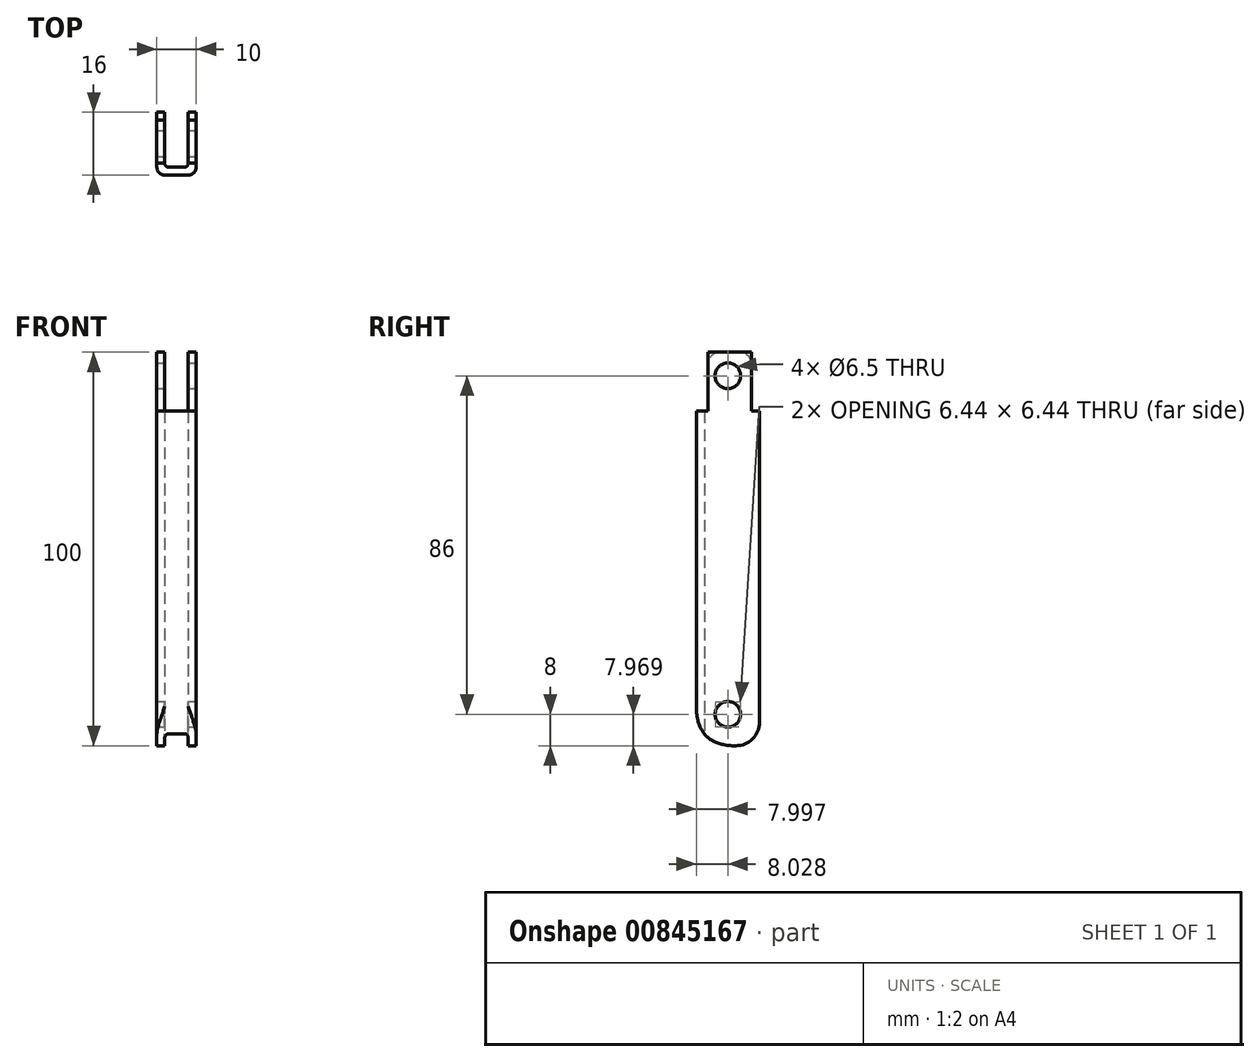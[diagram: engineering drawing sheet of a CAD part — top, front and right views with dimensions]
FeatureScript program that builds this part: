
annotation { "Feature Type Name" : "Feature", "Feature Type Description" : "" }
export const myFeature = defineFeature(function(context is Context, id is Id, definition is map)
    precondition{}
    {
        {
            var Q0;
            Q0=qCreatedBy(makeId("Top.planeOp"),FACE);
            var sketch = newSketch(context, id + "F0", { "sketchPlane" : qUnion([Q0])});
            skLineSegment(sketch, "E0.bottom", {"start": v(-5.2, -4.8) * mm, "end": v(-3.2, -4.8) * mm});
            skLineSegment(sketch, "E0.top", {"start": v(-3.2, -20.8) * mm, "end": v(2.8, -20.8) * mm});
            skLineSegment(sketch, "E0.left", {"start": v(-5.2, -4.8) * mm, "end": v(-5.2, -18.8) * mm});
            skLineSegment(sketch, "E0.right", {"start": v(4.8, -4.8) * mm, "end": v(4.8, -18.8) * mm});
            skLineSegment(sketch, "E1.top", {"start": v(-2.2, -18.8) * mm, "end": v(1.8, -18.8) * mm});
            skLineSegment(sketch, "E1.left", {"start": v(-3.2, -4.8) * mm, "end": v(-3.2, -17.8) * mm});
            skLineSegment(sketch, "E1.right", {"start": v(2.8, -4.8) * mm, "end": v(2.8, -17.8) * mm});
            skPoint(sketch, "E2.visualSharp", {"position": v(-3.2, -18.8) * mm});
            skArc(sketch, "E2.filletArc", {"start": v(-3.2, -17.8) * mm, "mid": v(-2.91, -18.5) * mm, "end": v(-2.2, -18.8) * mm});
            skPoint(sketch, "E3.visualSharp", {"position": v(2.8, -18.8) * mm});
            skArc(sketch, "E3.filletArc", {"start": v(1.8, -18.8) * mm, "mid": v(2.5, -18.5) * mm, "end": v(2.8, -17.8) * mm});
            skPoint(sketch, "E4.visualSharp", {"position": v(-5.2, -20.8) * mm});
            skArc(sketch, "E4.filletArc", {"start": v(-5.2, -18.8) * mm, "mid": v(-4.62, -20.2) * mm, "end": v(-3.2, -20.8) * mm});
            skPoint(sketch, "E5.visualSharp", {"position": v(4.8, -20.8) * mm});
            skArc(sketch, "E5.filletArc", {"start": v(2.8, -20.8) * mm, "mid": v(4.21, -20.2) * mm, "end": v(4.8, -18.8) * mm});
            skLineSegment(sketch, "E6.trimOffspring", {"start": v(2.8, -4.8) * mm, "end": v(4.8, -4.8) * mm});
            skSolve(sketch);
        }
        {
            var Q0;
            Q0 = qSketchRegion(id + "F0", true);
            extrude(context, id + "F1", {"entities" : qUnion([Q0]), "depth" : 100 * mm, "offsetDistance" : 25 * mm});
        }
        {
            var Q0;
            Q0=makeQuery(id+"F1.opExtrude","SWEPT_FACE",FACE,{"disambiguationData":[OSD([sQuery(id+"F0.wireOp",EDGE,"E0.right")])]});
            var sketch = newSketch(context, id + "F2", { "sketchPlane" : qUnion([Q0])});
            skCircle(sketch, "E7", {"center": v(-12.8, 94) * mm, "radius": 3.25 * mm});
            skLineSegment(sketch, "E8", {"start": v(-12.8, 94) * mm, "end": v(-12.8, 100) * mm});
            skLineSegment(sketch, "E9.bottom", {"start": v(-4.8, 100) * mm, "end": v(-6.8, 100) * mm});
            skLineSegment(sketch, "E9.top", {"start": v(-4.8, 85) * mm, "end": v(-6.8, 85) * mm});
            skLineSegment(sketch, "E9.left", {"start": v(-4.8, 100) * mm, "end": v(-4.8, 85) * mm});
            skLineSegment(sketch, "E9.right", {"start": v(-6.8, 100) * mm, "end": v(-6.8, 85) * mm});
            skLineSegment(sketch, "E10.bottom", {"start": v(-20.8, 100) * mm, "end": v(-17.8, 100) * mm});
            skLineSegment(sketch, "E10.top", {"start": v(-20.8, 85) * mm, "end": v(-17.8, 85) * mm});
            skLineSegment(sketch, "E10.left", {"start": v(-20.8, 100) * mm, "end": v(-20.8, 85) * mm});
            skLineSegment(sketch, "E10.right", {"start": v(-17.8, 100) * mm, "end": v(-17.8, 85) * mm});
            skCircle(sketch, "E11", {"center": v(-12.8, 8) * mm, "radius": 3.25 * mm});
            skLineSegment(sketch, "E12", {"start": v(-12.8, 8) * mm, "end": v(-12.8, 0) * mm});
            skSolve(sketch);
        }
        {
            var Q0;
            Q0 = qSketchRegion(id + "F2", true);
            extrude(context, id + "F3", {"entities" : qUnion([Q0]), "operationType" : NewBodyOperationType.REMOVE, "oppositeDirection" : true, "depth" : 25 * mm, "offsetDistance" : 25 * mm});
        }
        {
            var Q0;
            {var subQ1=sQuery(id+"F0.wireOp",EDGE,"E0.right");var subQ2=sQuery(id+"F2.wireOp",EDGE,"E9.right");Q0=makeQuery(id+"F3.boolean.opBoolean","COPY",EDGE,{"disambiguationData":[TD([makeQuery(id+"F1.opExtrude","SWEPT_FACE",FACE,{"disambiguationData":[OSD([subQ1])]})])],"derivedFrom":makeQuery(id+"F3.opExtrude","SWEPT_EDGE",EDGE,{"disambiguationData":[OSD([subQ1,sQuery(id+"F2.wireOp",EDGE,"E9.bottom"),subQ2])]})});}
            var Q1;
            {var subQ1=sQuery(id+"F0.wireOp",EDGE,"E0.right");var subQ2=sQuery(id+"F2.wireOp",EDGE,"E10.right");Q1=makeQuery(id+"F3.boolean.opBoolean","COPY",EDGE,{"disambiguationData":[TD([makeQuery(id+"F1.opExtrude","SWEPT_FACE",FACE,{"disambiguationData":[OSD([subQ1])]})])],"derivedFrom":makeQuery(id+"F3.opExtrude","SWEPT_EDGE",EDGE,{"disambiguationData":[OSD([subQ1,sQuery(id+"F2.wireOp",EDGE,"E10.bottom"),subQ2])]})});}
            var Q2;
            {var subQ1=sQuery(id+"F0.wireOp",EDGE,"E0.right");var subQ2=sQuery(id+"F0.wireOp",EDGE,"E0.left");var subQ3=sQuery(id+"F2.wireOp",EDGE,"E9.right");Q2=makeQuery(id+"F3.boolean.opBoolean","COPY",EDGE,{"disambiguationData":[TD([makeQuery(id+"F1.opExtrude","SWEPT_FACE",FACE,{"disambiguationData":[OSD([subQ2])]})])],"derivedFrom":makeQuery(id+"F3.opExtrude","SWEPT_EDGE",EDGE,{"disambiguationData":[OSD([subQ1,sQuery(id+"F2.wireOp",EDGE,"E9.bottom"),subQ3])]})});}
            var Q3;
            {var subQ1=sQuery(id+"F0.wireOp",EDGE,"E0.right");var subQ2=sQuery(id+"F0.wireOp",EDGE,"E0.left");var subQ3=sQuery(id+"F2.wireOp",EDGE,"E10.right");Q3=makeQuery(id+"F3.boolean.opBoolean","COPY",EDGE,{"disambiguationData":[TD([makeQuery(id+"F1.opExtrude","SWEPT_FACE",FACE,{"disambiguationData":[OSD([subQ2])]})])],"derivedFrom":makeQuery(id+"F3.opExtrude","SWEPT_EDGE",EDGE,{"disambiguationData":[OSD([subQ1,sQuery(id+"F2.wireOp",EDGE,"E10.bottom"),subQ3])]})});}
            fillet(context, id + "F4", {"entities" : qUnion([Q0, Q1, Q2, Q3]), "radius" : 3 * mm, "tangentPropagation" : true, "allowEdgeOverflow" : false});
        }
        {
            var Q0;
            Q0=makeQuery(id+"F1.opExtrude","CAP_EDGE",EDGE,{"disambiguationData":[OSD([sQuery(id+"F0.wireOp",EDGE,"E0.top")])],"isStart":true});
            fillet(context, id + "F5", {"entities" : qUnion([Q0]), "radius" : 10 * mm, "rho" : 0.5, "crossSection" : FilletCrossSection.CONIC, "allowEdgeOverflow" : false});
        }
        {
            var Q0;
            Q0=makeQuery(id+"F1.opExtrude","CAP_EDGE",EDGE,{"disambiguationData":[OSD([sQuery(id+"F0.wireOp",EDGE,"E6.trimOffspring")])],"isStart":true});
            var Q1;
            Q1=makeQuery(id+"F1.opExtrude","CAP_EDGE",EDGE,{"disambiguationData":[OSD([sQuery(id+"F0.wireOp",EDGE,"E0.bottom")])],"isStart":true});
            fillet(context, id + "F6", {"entities" : qUnion([Q0, Q1]), "radius" : 6 * mm, "tangentPropagation" : true, "allowEdgeOverflow" : false});
        }
    });
